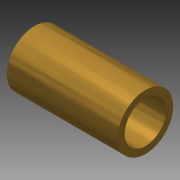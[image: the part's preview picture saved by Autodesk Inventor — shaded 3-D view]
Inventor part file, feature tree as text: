
AUTODESK INVENTOR PART (.ipt)
format: ipt  version: 2015 SP1 (Build 190203100, 203)  size: 102,912 bytes
history: native  units: in
note: dims shown in document units (in); Inventor stores cm internally (conversion verified against a paired STEP export)
features: extrude x1, sketch x1
ambient origin geometry x8: Origin, YZ Plane, XZ Plane, XY Plane, X Axis, Y Axis, Z Axis, Center Point
bodies: Solid1 (feature_tree)
feature tree (2):
  extrude  "Extrusion1"  Depth=1.0in
  sketch  "Sketch1"  dims[d0=0.375in d1=0.5in d2=1.0in d3=0.0in]
